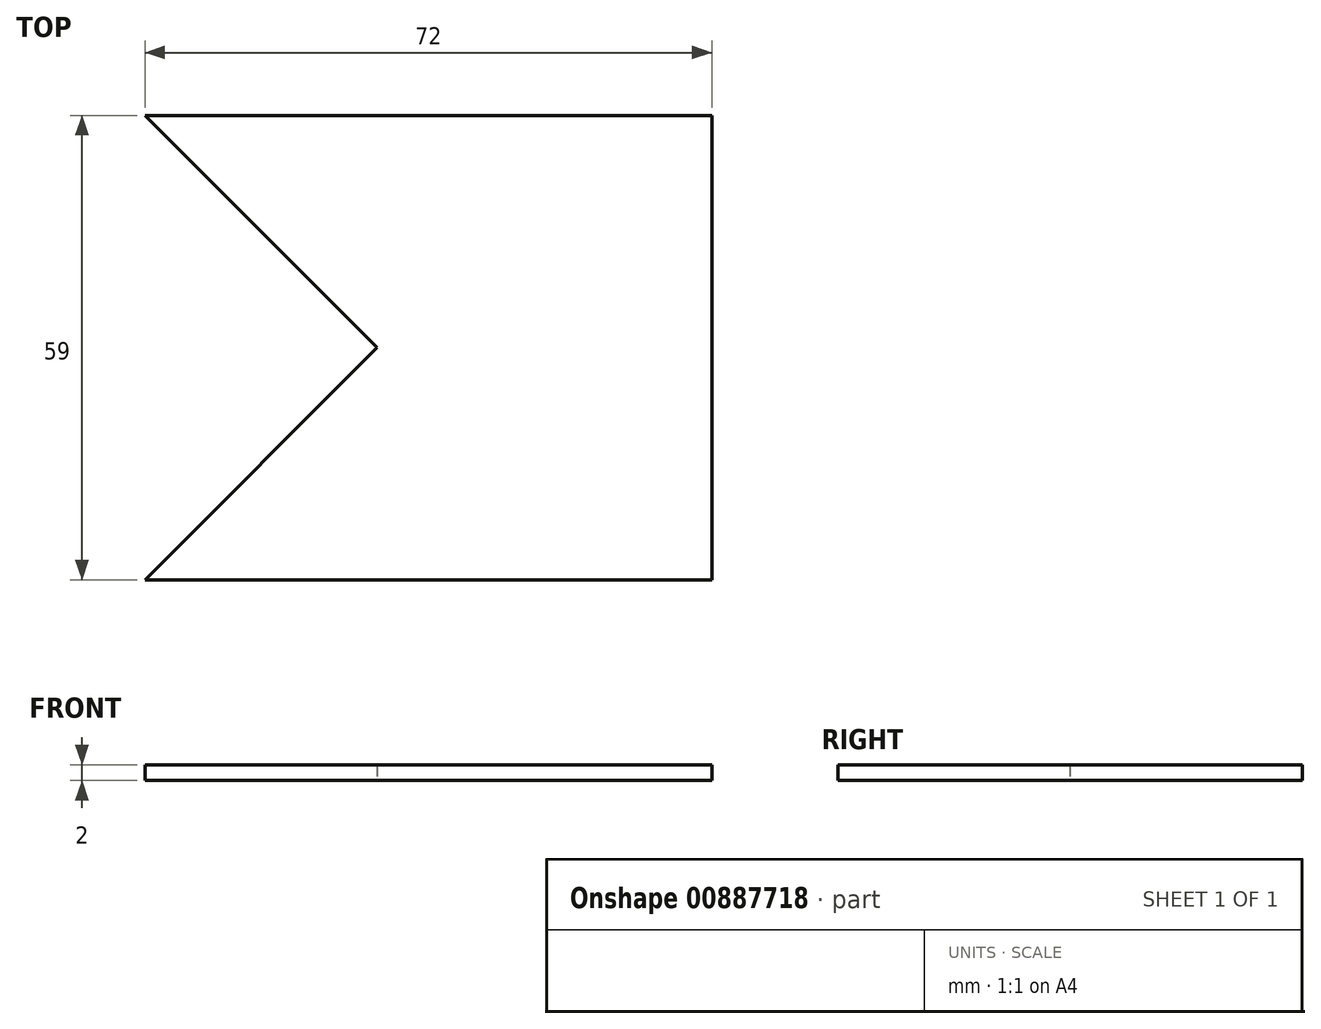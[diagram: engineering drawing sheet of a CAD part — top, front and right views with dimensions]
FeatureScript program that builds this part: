
annotation { "Feature Type Name" : "Feature", "Feature Type Description" : "" }
export const myFeature = defineFeature(function(context is Context, id is Id, definition is map)
    precondition{}
    {
        {
            var Q0;
            Q0=qCreatedBy(makeId("Top.planeOp"),FACE);
            var sketch = newSketch(context, id + "F0", { "sketchPlane" : qUnion([Q0])});
            skLineSegment(sketch, "E0.bottom", {"start": v(0, 0) * mm, "end": v(72, 0) * mm});
            skLineSegment(sketch, "E0.top", {"start": v(0, 59) * mm, "end": v(72, 59) * mm});
            skLineSegment(sketch, "E0.left", {"start": v(0, 0) * mm, "end": v(0, 59) * mm});
            skLineSegment(sketch, "E0.right", {"start": v(72, 0) * mm, "end": v(72, 59) * mm});
            skSolve(sketch);
        }
        {
            var Q0;
            Q0=makeQuery(id+"F0.imprint","IMPRINT",FACE,{"disambiguationData":[TD([[makeQuery(id+"F0.imprint","IMPRINT",EDGE,{"derivedFrom":sQuery(id+"F0.wireOp",EDGE,"E0.bottom")}),1.0]])]});
            extrude(context, id + "F1", {"entities" : qUnion([Q0]), "depth" : 2 * mm, "offsetDistance" : 25 * mm});
        }
        {
            var Q0;
            Q0=qCreatedBy(makeId("Top.planeOp"),FACE);
            var sketch = newSketch(context, id + "F2", { "sketchPlane" : qUnion([Q0])});
            skLineSegment(sketch, "E1", {"start": v(0, 0) * mm, "end": v(29.5, 29.5) * mm});
            skLineSegment(sketch, "E2", {"start": v(29.5, 29.5) * mm, "end": v(0, 59) * mm});
            skLineSegment(sketch, "E3", {"start": v(0, 59) * mm, "end": v(0, 0) * mm});
            skSolve(sketch);
        }
        {
            var Q0;
            Q0=makeQuery(id+"F2.imprint","IMPRINT",FACE,{"disambiguationData":[TD([[makeQuery(id+"F2.imprint","IMPRINT",EDGE,{"derivedFrom":sQuery(id+"F2.wireOp",EDGE,"E1")}),1.0]])]});
            extrude(context, id + "F3", {"entities" : qUnion([Q0]), "operationType" : NewBodyOperationType.REMOVE, "depth" : 5 * mm, "offsetDistance" : 25 * mm});
        }
    });
